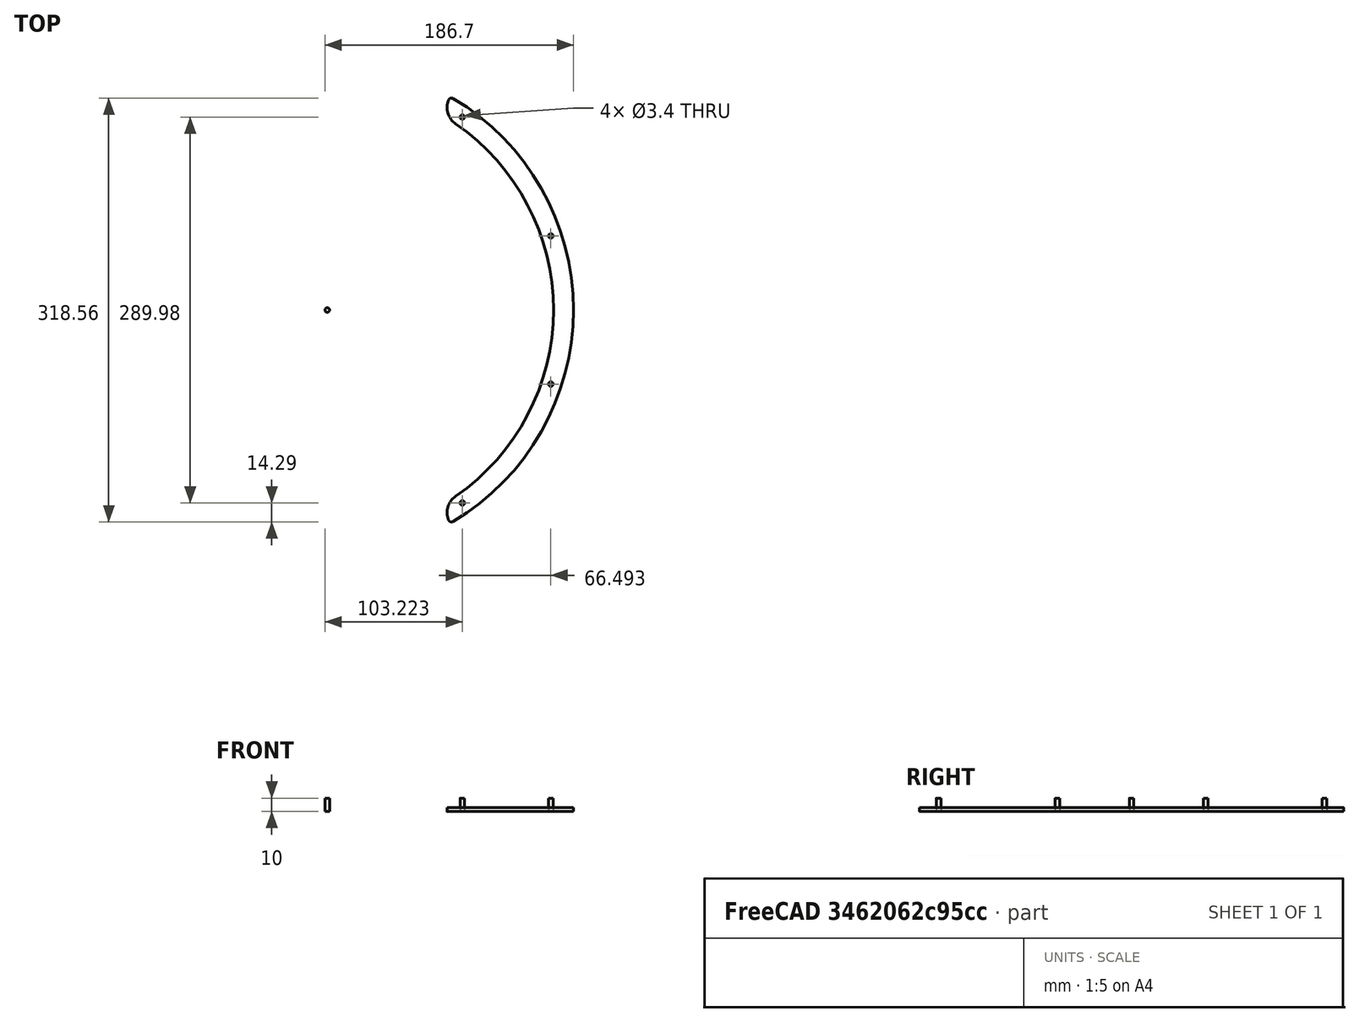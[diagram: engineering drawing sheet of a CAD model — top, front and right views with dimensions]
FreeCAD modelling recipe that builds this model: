
FCSTD DOCUMENT  (FreeCAD 1.1R38827 (Git))
Label: composit_stand3_basin_holder_model
License: All rights reserved
LicenseURL: http://en.wikipedia.org/wiki/All_rights_reserved
objects: PartDesign::SubShapeBinder×2, Part::FeaturePython×2, Part::Mirroring×1, PartDesign::Pad×1, Part::Cylinder×1, App::Link×1, Part::MultiFuse×1, PartDesign::Boolean×1, PartDesign::CoordinateSystem×1, PartDesign::Body×1
note: 14 computed .brp shape members not serialized (recipe doc carries the construction recipe); baked Part::Feature solids carry a one-line shape summary decoded from their .brp
EXTERNAL_REF file=composit_stand3_basin_holder_main.FCStd obj=Sketch
EXTERNAL_REF file=composit_stand3_basin_holder_main.FCStd obj=Join

FEATURE [PartDesign::SubShapeBinder] Binder
  BindCopyOnChange = 0
  BindMode = 0
  ClaimChildren = true
  Fuse = false
  MakeFace = true
  OffsetFill = false
  OffsetIntersection = false
  OffsetJoinType = 0
  OffsetOpenResult = false
  PartialLoad = false
  Relative = false
  Support = -> [<external composit_stand3_basin_holder_main.FCStd>#Sketch]
  _Version = 2
FEATURE [Part::Mirroring] Part__Mirroring  label="Binder (Mirror #1)"
  Base = (0,0,0)
  Normal = (0,1,0)
  Source = -> Binder
FEATURE [Part::FeaturePython] Connect  # WARN: FeaturePython — macro-defined, semantics opaque (R4)
  Objects = -> [Binder,Part__Mirroring]
  Tolerance = 0
FEATURE [PartDesign::SubShapeBinder] Binder001
  BindCopyOnChange = 0
  BindMode = 0
  ClaimChildren = true
  Context = -> Body [Binder001.]
  Fuse = false
  MakeFace = true
  OffsetFill = false
  OffsetIntersection = false
  OffsetJoinType = 0
  OffsetOpenResult = false
  PartialLoad = false
  Relative = true
  Support = -> [Connect]
  _Version = 2
FEATURE [PartDesign::Pad] Pad
  Direction = (0,0,1)
  Length = 3
  Length2 = 10
  Profile = -> Binder001
  Suppressed = false
  Type = 0
FEATURE [Part::Cylinder] Cylinder
  Angle = 360
  AttacherType = Attacher::AttachEngine3D
  FirstAngle = 0
  Height = 10
  Radius = 1.7
  SecondAngle = 0
FEATURE [App::Link] Link  label="holes"
  LinkedObject = -> <external composit_stand3_basin_holder_main.FCStd>#Join
FEATURE [Part::FeaturePython] Populate  label="Populate holes with Cylinder"  # WARN: FeaturePython — macro-defined, semantics opaque (R4)
  Copying = 0
  ExposePlacement = false
  MarkerShape = 1
  MarkerSize = 0
  NumElements = 0
  Object = -> Cylinder
  OutputCompounding = 1
  PlacementsTo = -> Link
  Referencing = 0
  Type = lattice2PopulateCopies.LatticePopulateCopies
  isLattice = 0
FEATURE [Part::MultiFuse] Fusion
  Shapes = -> [Populate]
FEATURE [PartDesign::Boolean] Boolean
  BaseFeature = -> Pad
  Group = -> [Fusion]
  Suppressed = false
  Type = 1
  UsePlacement = true
FEATURE [PartDesign::CoordinateSystem] Local_CS
  AttacherType = Attacher::AttachEngine3D
  AttachmentSupport = -> [XY_Plane]
  MapMode = 5
FEATURE [PartDesign::Body] Body  label="basin_holder"
  AllowCompound = false
  Group = -> [Binder001,Pad,Boolean,Local_CS]
  Origin = -> Origin
  Tip = -> Boolean
